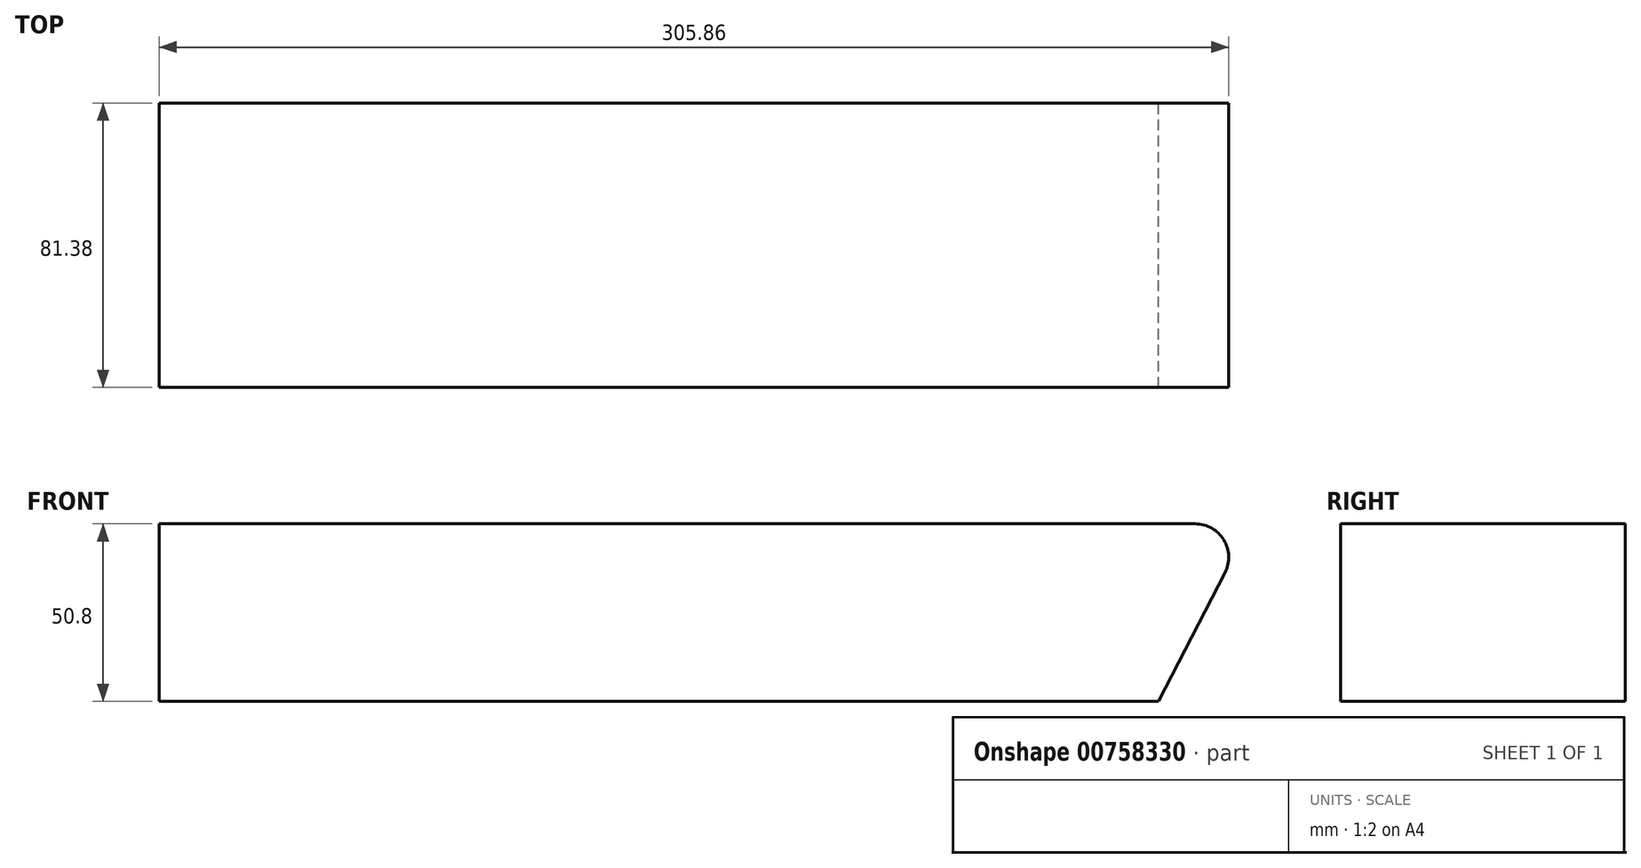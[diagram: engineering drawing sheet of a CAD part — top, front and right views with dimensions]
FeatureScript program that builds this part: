
annotation { "Feature Type Name" : "Feature", "Feature Type Description" : "" }
export const myFeature = defineFeature(function(context is Context, id is Id, definition is map)
    precondition{}
    {
        {
            var Q0;
            Q0=qCreatedBy(makeId("Front.planeOp"),FACE);
            var sketch = newSketch(context, id + "F0", { "sketchPlane" : qUnion([Q0])});
            skLineSegment(sketch, "E0", {"start": v(-234.17, 50.8) * mm, "end": v(-234.17, 0) * mm});
            skLineSegment(sketch, "E1", {"start": v(-234.17, 0) * mm, "end": v(51.58, 0) * mm});
            skLineSegment(sketch, "E2", {"start": v(-234.17, 50.8) * mm, "end": v(62.16, 50.8) * mm});
            skLineSegment(sketch, "E3", {"start": v(70.63, 36.9) * mm, "end": v(51.58, 0) * mm});
            skArc(sketch, "E4.filletArc", {"start": v(70.63, 36.9) * mm, "mid": v(70.3, 46.23) * mm, "end": v(62.16, 50.8) * mm});
            skSolve(sketch);
        }
        {
            var Q0;
            Q0 = qSketchRegion(id + "F0", true);
            extrude(context, id + "F1", {"entities" : qUnion([Q0]), "depth" : (81 + (3 / 8)) * mm, "offsetDistance" : 25.4 * mm});
        }
    });
